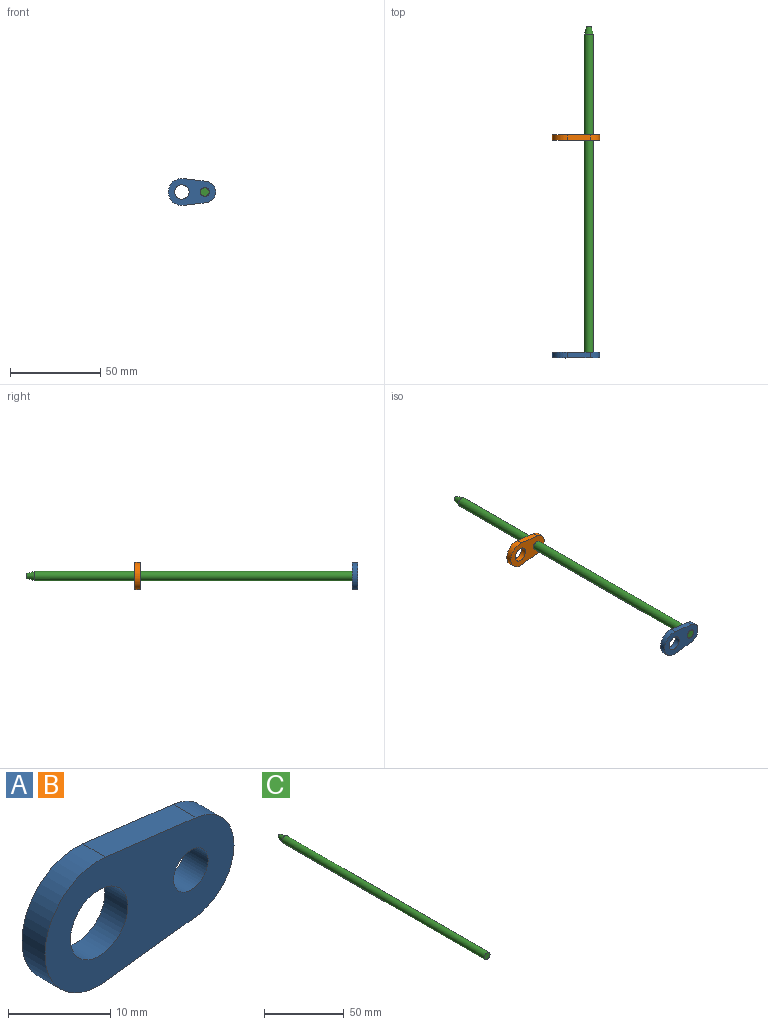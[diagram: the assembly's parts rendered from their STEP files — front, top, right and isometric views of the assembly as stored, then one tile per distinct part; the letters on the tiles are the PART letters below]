
ASSEMBLY  parts=3 mates=2
PART A: 8 faces, bbox 26.2x3.2x15 mm
  f0: plane 12.52x3.18mm, normal (0.12,0,-0.99), area 40mm2, adj f1,f5,f6,f7
  f1: cylinder r=5.97mm len=11.85mm, axis (0,1,0), area 55mm2, adj f0,f2,f6,f7
  f2: plane 12.52x3.18mm, normal (0.12,0,0.99), area 40mm2, adj f1,f5,f6,f7
  f3: cylinder r=2.38mm len=4.76mm, axis (0,1,0), area 47.5mm2, adj f6,f7
  f4: cylinder r=3.97mm len=7.94mm, axis (0,1,0), area 79.2mm2, adj f6,f7
  f5: cylinder r=7.49mm len=14.99mm, axis (0,1,0), area 80.5mm2, adj f0,f2,f6,f7
  f6: plane 26.16x14.99mm, normal (0,-1,0), area 249.1mm2, adj f0,f1,f2,f3,f4,f5
  f7: plane 26.16x14.99mm, normal (0,1,0), area 249.1mm2, adj f0,f1,f2,f3,f4,f5
PART B: same geometry as A
PART C: 4 faces, bbox 5.1x184.2x5.1 mm
  f0: cylinder r=2.54mm len=179.39mm, axis (0,1,0), area 2862.9mm2, adj f1,f3
  f1: plane 5.08x5.08mm, normal (0,-1,0), area 20.3mm2, adj f0
  f2: plane 2.53x2.53mm, normal (0,1,0), area 5mm2, adj f3
  f3: cone r=2.54mm half-angle=15deg, axis (0,-1,0), area 58.9mm2, adj f0,f2
PLACE A t=(-125.32,-203.84,-8.34)mm
PLACE B t=(-125.32,-83.19,-8.34)mm
PLACE C t=(-112.62,-22.86,-8.34)mm fixed
MATE fastened A.f1 <-> C.f0  axis (0,-1,0) through (-112.62,-207.01,-8.34)mm
MATE slider C.f0 <-> B.f1  axis (0,-1,0) through (-112.62,-207.01,-8.34)mm
